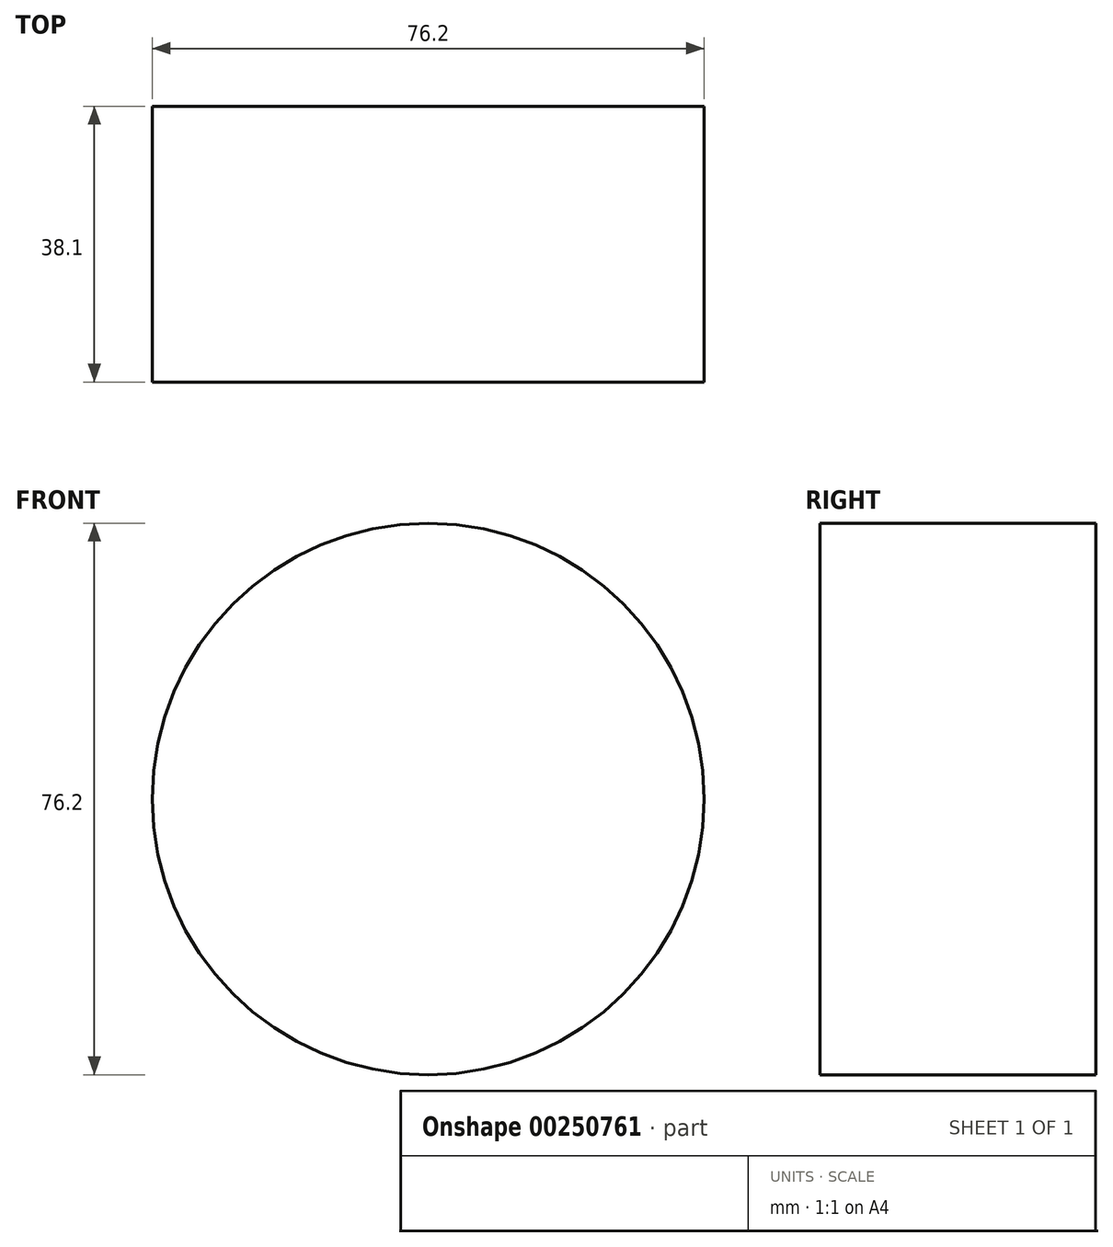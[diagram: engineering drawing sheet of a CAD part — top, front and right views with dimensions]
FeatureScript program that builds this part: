
annotation { "Feature Type Name" : "Feature", "Feature Type Description" : "" }
export const myFeature = defineFeature(function(context is Context, id is Id, definition is map)
    precondition{}
    {
        {
            var Q0;
            Q0=qCreatedBy(makeId("Front.planeOp"),FACE);
            var sketch = newSketch(context, id + "F0", { "sketchPlane" : qUnion([Q0])});
            skCircle(sketch, "E0", {"center": v(0, 0) * mm, "radius": 38.1 * mm});
            skSolve(sketch);
        }
        {
            var Q0;
            Q0=makeQuery(id+"F0.imprint","IMPRINT",FACE,{"disambiguationData":[TD([[makeQuery(id+"F0.imprint","IMPRINT",EDGE,{"derivedFrom":sQuery(id+"F0.wireOp",EDGE,"E0")}),1.0]])]});
            extrude(context, id + "F1", {"entities" : qUnion([Q0]), "oppositeDirection" : true, "depth" : 38.1 * mm});
        }
    });
